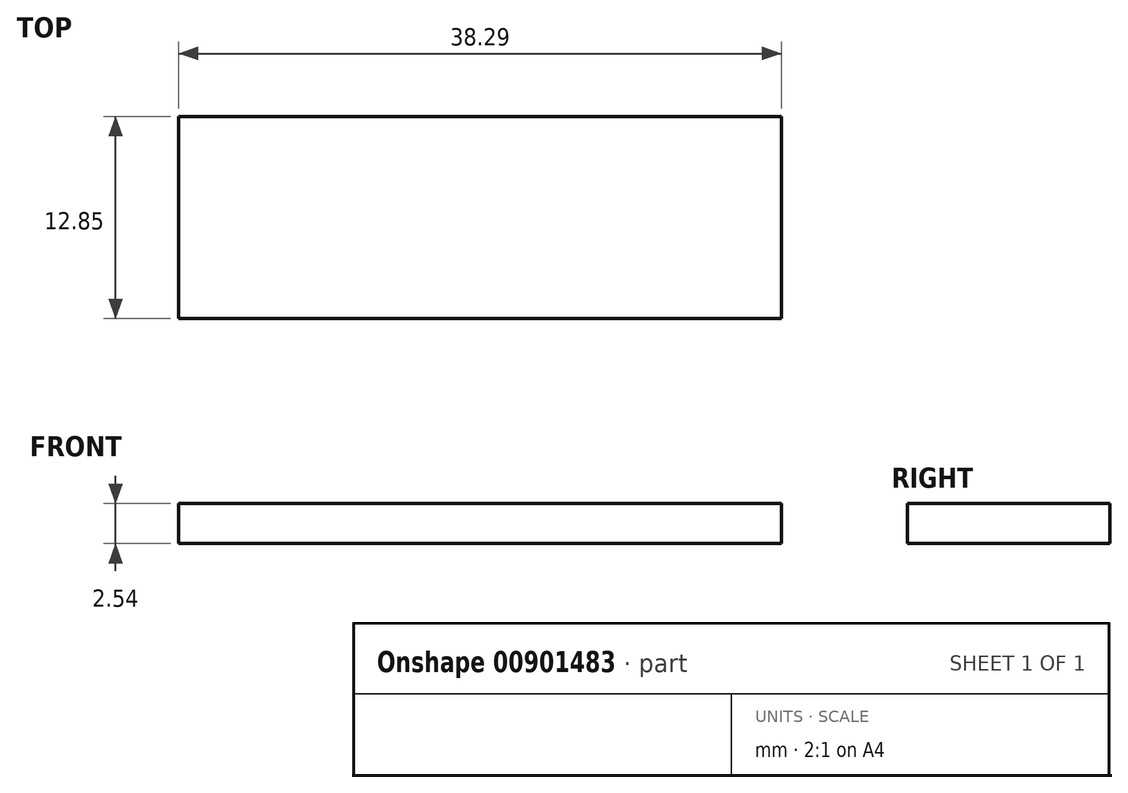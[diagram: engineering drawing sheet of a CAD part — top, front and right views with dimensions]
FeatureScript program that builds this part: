
annotation { "Feature Type Name" : "Feature", "Feature Type Description" : "" }
export const myFeature = defineFeature(function(context is Context, id is Id, definition is map)
    precondition{}
    {
        {
            var Q0;
            Q0=qCreatedBy(makeId("Top.planeOp"),FACE);
            var sketch = newSketch(context, id + "F0", { "sketchPlane" : qUnion([Q0])});
            skLineSegment(sketch, "E0.bottom", {"start": v(0, 0) * mm, "end": v(38.3, 0) * mm});
            skLineSegment(sketch, "E0.top", {"start": v(0, -12.85) * mm, "end": v(38.3, -12.85) * mm});
            skLineSegment(sketch, "E0.left", {"start": v(0, 0) * mm, "end": v(0, -12.85) * mm});
            skLineSegment(sketch, "E0.right", {"start": v(38.3, 0) * mm, "end": v(38.3, -12.85) * mm});
            skSolve(sketch);
        }
        {
            var Q0;
            Q0 = qSketchRegion(id + "F0", true);
            extrude(context, id + "F1", {"entities" : qUnion([Q0]), "depth" : 2.54 * mm, "offsetDistance" : 25.4 * mm});
        }
    });
